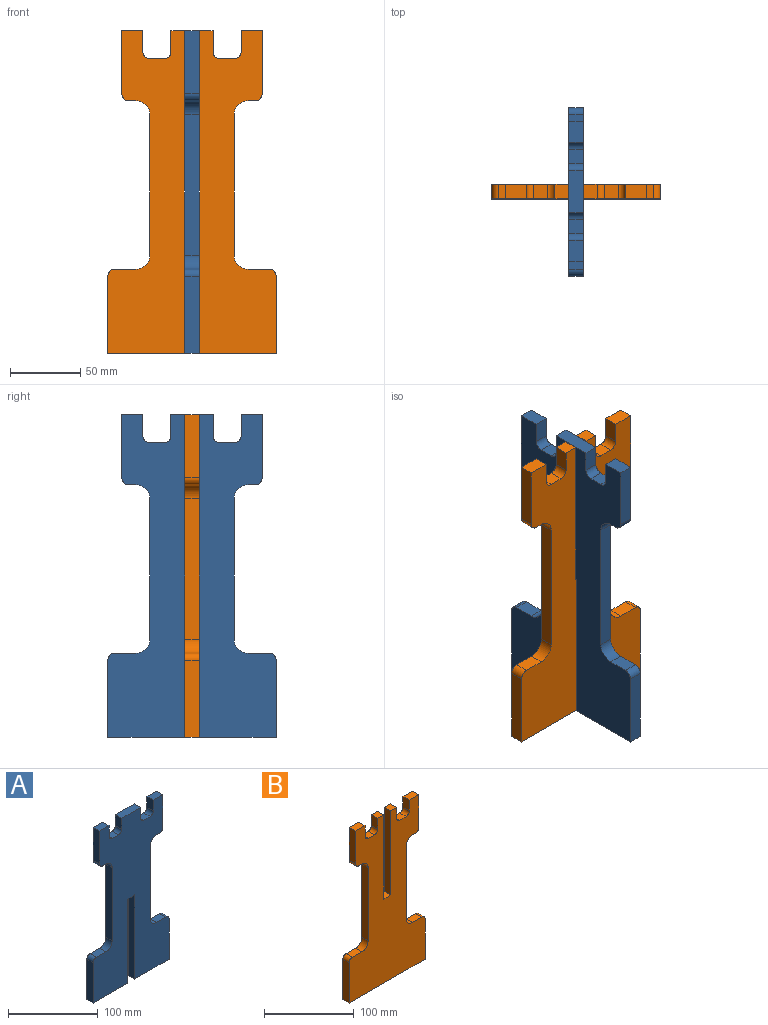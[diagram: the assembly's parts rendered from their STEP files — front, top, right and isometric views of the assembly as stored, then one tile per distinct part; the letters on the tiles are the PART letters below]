
ASSEMBLY  parts=2 mates=1
PART A: 38 faces, bbox 120x10x230 mm
  f0: plane 115x10mm, normal (1,0,0), area 1150mm2, adj f1,f35,f36,f37
  f1: plane 11x10mm, normal (0,0,-1), area 110mm2, adj f0,f2,f36,f37
  f2: plane 115x10mm, normal (-1,0,0), area 1150mm2, adj f1,f3,f36,f37
  f3: plane 54.5x10mm, normal (0,0,-1), area 545mm2, adj f2,f4,f36,f37
  f4: plane 55x10mm, normal (1,0,0), area 550mm2, adj f3,f5,f36,f37
  f5: cylinder r=5mm len=10mm, axis (0,1,0), area 78.5mm2, adj f4,f6,f36,f37
  f6: plane 15x10mm, normal (0,0,1), area 150mm2, adj f5,f7,f36,f37
  f7: cylinder r=10mm len=10mm, axis (0,1,0), area 157.1mm2, adj f6,f8,f36,f37
  f8: plane 100x10mm, normal (1,0,0), area 1000mm2, adj f7,f9,f36,f37
  f9: cylinder r=10mm len=10mm, axis (0,1,0), area 157.1mm2, adj f8,f10,f36,f37
  f10: plane 10x5mm, normal (0,0,-1), area 50mm2, adj f9,f11,f36,f37
  f11: cylinder r=5mm len=10mm, axis (0,1,0), area 78.5mm2, adj f10,f12,f36,f37
  f12: plane 45x10mm, normal (1,0,0), area 450mm2, adj f11,f13,f36,f37
  f13: plane 15x10mm, normal (0,0,1), area 150mm2, adj f12,f14,f36,f37
  f14: plane 15x10mm, normal (-1,0,0), area 150mm2, adj f13,f15,f36,f37
  f15: cylinder r=5mm len=10mm, axis (0,1,0), area 78.5mm2, adj f14,f16,f36,f37
  f16: plane 10x10mm, normal (0,0,1), area 100mm2, adj f15,f17,f36,f37
  f17: cylinder r=5mm len=10mm, axis (0,1,0), area 78.5mm2, adj f16,f18,f36,f37
  f18: plane 15x10mm, normal (1,0,0), area 150mm2, adj f17,f19,f36,f37
  f19: plane 30x10mm, normal (0,0,1), area 300mm2, adj f18,f20,f36,f37
  f20: plane 15x10mm, normal (-1,0,0), area 150mm2, adj f19,f21,f36,f37
  f21: cylinder r=5mm len=10mm, axis (0,1,0), area 78.5mm2, adj f20,f22,f36,f37
  f22: plane 10x10mm, normal (0,0,1), area 100mm2, adj f21,f23,f36,f37
  f23: cylinder r=5mm len=10mm, axis (0,1,0), area 78.5mm2, adj f22,f24,f36,f37
  f24: plane 15x10mm, normal (1,0,0), area 150mm2, adj f23,f25,f36,f37
  f25: plane 15x10mm, normal (0,0,1), area 150mm2, adj f24,f26,f36,f37
  f26: plane 45x10mm, normal (-1,0,0), area 450mm2, adj f25,f27,f36,f37
  f27: cylinder r=5mm len=10mm, axis (0,1,0), area 78.5mm2, adj f26,f28,f36,f37
  f28: plane 10x5mm, normal (0,0,-1), area 50mm2, adj f27,f29,f36,f37
  f29: cylinder r=10mm len=10mm, axis (0,1,0), area 157.1mm2, adj f28,f30,f36,f37
  f30: plane 100x10mm, normal (-1,0,0), area 1000mm2, adj f29,f31,f36,f37
  f31: cylinder r=10mm len=10mm, axis (0,1,0), area 157.1mm2, adj f30,f32,f36,f37
  f32: plane 15x10mm, normal (0,0,1), area 150mm2, adj f31,f33,f36,f37
  f33: cylinder r=5mm len=10mm, axis (0,1,0), area 78.5mm2, adj f32,f34,f36,f37
  f34: plane 55x10mm, normal (-1,0,0), area 550mm2, adj f33,f35,f36,f37
  f35: plane 54.5x10mm, normal (0,0,-1), area 545mm2, adj f0,f34,f36,f37
  f36: plane 230x120mm, normal (0,-1,0), area 17420.8mm2, adj f0,f1,f2,f3,f4,f5,f6,f7
  f37: plane 230x120mm, normal (0,1,0), area 17420.8mm2, adj f0,f1,f2,f3,f4,f5,f6,f7
PART B: 38 faces, bbox 120x10x230 mm
  f0: plane 55x10mm, normal (-1,0,0), area 550mm2, adj f1,f35,f36,f37
  f1: plane 120x10mm, normal (0,0,-1), area 1200mm2, adj f0,f2,f36,f37
  f2: plane 55x10mm, normal (1,0,0), area 550mm2, adj f1,f3,f36,f37
  f3: cylinder r=5mm len=10mm, axis (0,-1,0), area 78.5mm2, adj f2,f4,f36,f37
  f4: plane 15x10mm, normal (0,0,1), area 150mm2, adj f3,f5,f36,f37
  f5: cylinder r=10mm len=10mm, axis (0,-1,0), area 157.1mm2, adj f4,f6,f36,f37
  f6: plane 100x10mm, normal (1,0,0), area 1000mm2, adj f5,f7,f36,f37
  f7: cylinder r=10mm len=10mm, axis (0,-1,0), area 157.1mm2, adj f6,f8,f36,f37
  f8: plane 10x5mm, normal (0,0,-1), area 50mm2, adj f7,f9,f36,f37
  f9: cylinder r=5mm len=10mm, axis (0,-1,0), area 78.5mm2, adj f8,f10,f36,f37
  f10: plane 45x10mm, normal (1,0,0), area 450mm2, adj f9,f11,f36,f37
  f11: plane 15x10mm, normal (0,0,1), area 150mm2, adj f10,f12,f36,f37
  f12: plane 15x10mm, normal (-1,0,0), area 150mm2, adj f11,f13,f36,f37
  f13: cylinder r=5mm len=10mm, axis (0,-1,0), area 78.5mm2, adj f12,f14,f36,f37
  f14: plane 10x10mm, normal (0,0,1), area 100mm2, adj f13,f15,f36,f37
  f15: cylinder r=5mm len=10mm, axis (0,-1,0), area 78.5mm2, adj f14,f16,f36,f37
  f16: plane 15x10mm, normal (1,0,0), area 150mm2, adj f15,f17,f36,f37
  f17: plane 10x9.5mm, normal (0,0,1), area 95mm2, adj f16,f18,f36,f37
  f18: plane 115x10mm, normal (-1,0,0), area 1150mm2, adj f17,f19,f36,f37
  f19: plane 11x10mm, normal (0,0,1), area 110mm2, adj f18,f20,f36,f37
  f20: plane 115x10mm, normal (1,0,0), area 1150mm2, adj f19,f21,f36,f37
  f21: plane 10x9.5mm, normal (0,0,1), area 95mm2, adj f20,f22,f36,f37
  f22: plane 15x10mm, normal (-1,0,0), area 150mm2, adj f21,f23,f36,f37
  f23: cylinder r=5mm len=10mm, axis (0,-1,0), area 78.5mm2, adj f22,f24,f36,f37
  f24: plane 10x10mm, normal (0,0,1), area 100mm2, adj f23,f25,f36,f37
  f25: cylinder r=5mm len=10mm, axis (0,-1,0), area 78.5mm2, adj f24,f26,f36,f37
  f26: plane 15x10mm, normal (1,0,0), area 150mm2, adj f25,f27,f36,f37
  f27: plane 15x10mm, normal (0,0,1), area 150mm2, adj f26,f28,f36,f37
  f28: plane 45x10mm, normal (-1,0,0), area 450mm2, adj f27,f29,f36,f37
  f29: cylinder r=5mm len=10mm, axis (0,-1,0), area 78.5mm2, adj f28,f30,f36,f37
  f30: plane 10x5mm, normal (0,0,-1), area 50mm2, adj f29,f31,f36,f37
  f31: cylinder r=10mm len=10mm, axis (0,-1,0), area 157.1mm2, adj f30,f32,f36,f37
  f32: plane 100x10mm, normal (-1,0,0), area 1000mm2, adj f31,f33,f36,f37
  f33: cylinder r=10mm len=10mm, axis (0,-1,0), area 157.1mm2, adj f32,f34,f36,f37
  f34: plane 15x10mm, normal (0,0,1), area 150mm2, adj f33,f35,f36,f37
  f35: cylinder r=5mm len=10mm, axis (0,-1,0), area 78.5mm2, adj f0,f34,f36,f37
  f36: plane 230x120mm, normal (0,1,0), area 17420.8mm2, adj f0,f1,f2,f3,f4,f5,f6,f7
  f37: plane 230x120mm, normal (0,-1,0), area 17420.8mm2, adj f0,f1,f2,f3,f4,f5,f6,f7
PLACE A rot(axis=(0,0,1),90deg) t=(-5,5,0)mm
PLACE B at identity
MATE fastened A.f1 <-> B.f19  axis (0,0,-1) through (0,5,85)mm
